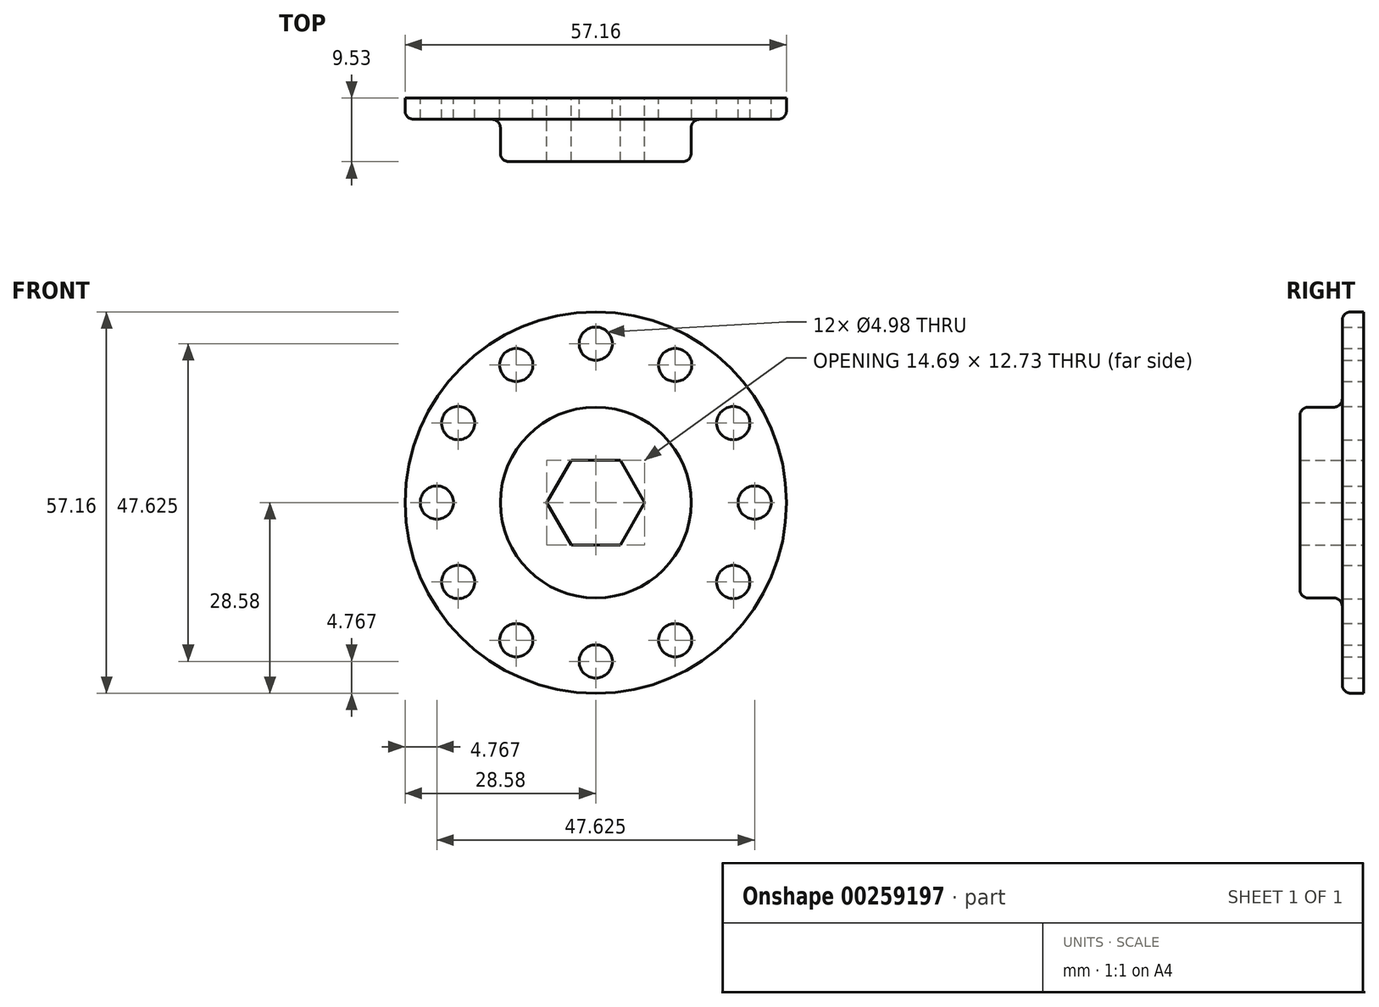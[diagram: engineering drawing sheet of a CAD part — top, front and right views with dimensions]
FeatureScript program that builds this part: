
annotation { "Feature Type Name" : "Feature", "Feature Type Description" : "" }
export const myFeature = defineFeature(function(context is Context, id is Id, definition is map)
    precondition{}
    {
        {
            var Q0;
            Q0=qCreatedBy(makeId("Front.planeOp"),FACE);
            var sketch = newSketch(context, id + "F0", { "sketchPlane" : qUnion([Q0])});
            skCircle(sketch, "E0", {"center": v(0, 0) * mm, "radius": 28.58 * mm});
            skCircle(sketch, "E1", {"center": v(0, 23.81) * mm, "radius": 2.49 * mm});
            skCircle(sketch, "E2.1.0", {"center": v(-11.9, 20.62) * mm, "radius": 2.49 * mm});
            skCircle(sketch, "E2.2.0", {"center": v(-20.62, 11.9) * mm, "radius": 2.49 * mm});
            skCircle(sketch, "E2.3.0", {"center": v(-23.81, 0) * mm, "radius": 2.49 * mm});
            skCircle(sketch, "E2.4.0", {"center": v(-20.62, -11.9) * mm, "radius": 2.49 * mm});
            skCircle(sketch, "E2.5.0", {"center": v(-11.9, -20.62) * mm, "radius": 2.49 * mm});
            skCircle(sketch, "E3", {"center": v(0, 0) * mm, "radius": 14.3 * mm});
            skLineSegment(sketch, "E4.0", {"start": v(-3.67, 6.36) * mm, "end": v(3.67, 6.36) * mm});
            skLineSegment(sketch, "E4.1", {"start": v(3.67, 6.36) * mm, "end": v(7.35, 0) * mm});
            skLineSegment(sketch, "E4.2", {"start": v(7.35, 0) * mm, "end": v(3.67, -6.36) * mm});
            skLineSegment(sketch, "E4.3", {"start": v(3.67, -6.36) * mm, "end": v(-3.67, -6.36) * mm});
            skLineSegment(sketch, "E4.4", {"start": v(-3.67, -6.36) * mm, "end": v(-7.35, 0) * mm});
            skLineSegment(sketch, "E4.5", {"start": v(-7.35, 0) * mm, "end": v(-3.67, 6.36) * mm});
            skPoint(sketch, "E4.0.midPoint", {"position": v(0, 6.36) * mm});
            skCircle(sketch, "E5.1.6.0", {"center": v(0, -23.81) * mm, "radius": 2.49 * mm});
            skCircle(sketch, "E5.1.7.0", {"center": v(11.9, -20.62) * mm, "radius": 2.49 * mm});
            skCircle(sketch, "E5.1.8.0", {"center": v(20.62, -11.9) * mm, "radius": 2.49 * mm});
            skCircle(sketch, "E5.1.9.0", {"center": v(23.81, 0) * mm, "radius": 2.49 * mm});
            skCircle(sketch, "E5.1.10.0", {"center": v(20.62, 11.9) * mm, "radius": 2.49 * mm});
            skCircle(sketch, "E5.1.11.0", {"center": v(11.9, 20.62) * mm, "radius": 2.49 * mm});
            skSolve(sketch);
        }
        {
            var Q0;
            Q0=qSketchRegion(id+"F0",true);
            var Q1;
            Q1=makeQuery(id+"F0.imprint","IMPRINT",FACE,{"disambiguationData":[TD([[makeQuery(id+"F0.imprint","IMPRINT",EDGE,{"derivedFrom":sQuery(id+"F0.wireOp",EDGE,"E3")}),1.0]])]});
            extrude(context, id + "F1", {"entities" : qUnion([Q0, Q1]), "depth" : 3.17 * mm});
        }
        {
            var Q0;
            Q0=makeQuery(id+"F0.imprint","IMPRINT",FACE,{"disambiguationData":[TD([[makeQuery(id+"F0.imprint","IMPRINT",EDGE,{"derivedFrom":sQuery(id+"F0.wireOp",EDGE,"E3")}),1.0]])]});
            extrude(context, id + "F2", {"entities" : qUnion([Q0]), "operationType" : NewBodyOperationType.ADD, "depth" : 9.52 * mm});
        }
        {
            var Q0;
            Q0=makeQuery(id+"F1.opExtrude","CAP_EDGE",EDGE,{"disambiguationData":[OSD([sQuery(id+"F0.wireOp",EDGE,"E0")])],"isStart":false});
            var Q1;
            Q1=makeQuery(id+"F2.opExtrude","CAP_EDGE",EDGE,{"disambiguationData":[OSD([sQuery(id+"F0.wireOp",EDGE,"E3")])],"isStart":false});
            var Q2;
            Q2=makeQuery(id+"F2.boolean.opBoolean","INTERSECT",EDGE,{"derivedFrom":[makeQuery(id+"F1.opExtrude","CAP_FACE",FACE,{"disambiguationData":[OSD([sQuery(id+"F0.wireOp",EDGE,"E0"),sQuery(id+"F0.wireOp",EDGE,"E1"),sQuery(id+"F0.wireOp",EDGE,"E2.1.0"),sQuery(id+"F0.wireOp",EDGE,"E2.2.0"),sQuery(id+"F0.wireOp",EDGE,"E2.3.0"),sQuery(id+"F0.wireOp",EDGE,"E2.4.0"),sQuery(id+"F0.wireOp",EDGE,"E2.5.0"),sQuery(id+"F0.wireOp",EDGE,"E4.0"),sQuery(id+"F0.wireOp",EDGE,"E4.1"),sQuery(id+"F0.wireOp",EDGE,"E4.2"),sQuery(id+"F0.wireOp",EDGE,"E4.3"),sQuery(id+"F0.wireOp",EDGE,"E4.4"),sQuery(id+"F0.wireOp",EDGE,"E4.5")])],"isStart":false}),makeQuery(id+"F2.opExtrude","SWEPT_FACE",FACE,{"disambiguationData":[OSD([sQuery(id+"F0.wireOp",EDGE,"E3")])]})]});
            fillet(context, id + "F3", {"entities" : qUnion([Q0, Q1, Q2]), "radius" : 1.27 * mm, "tangentPropagation" : true, "allowEdgeOverflow" : false});
        }
    });
